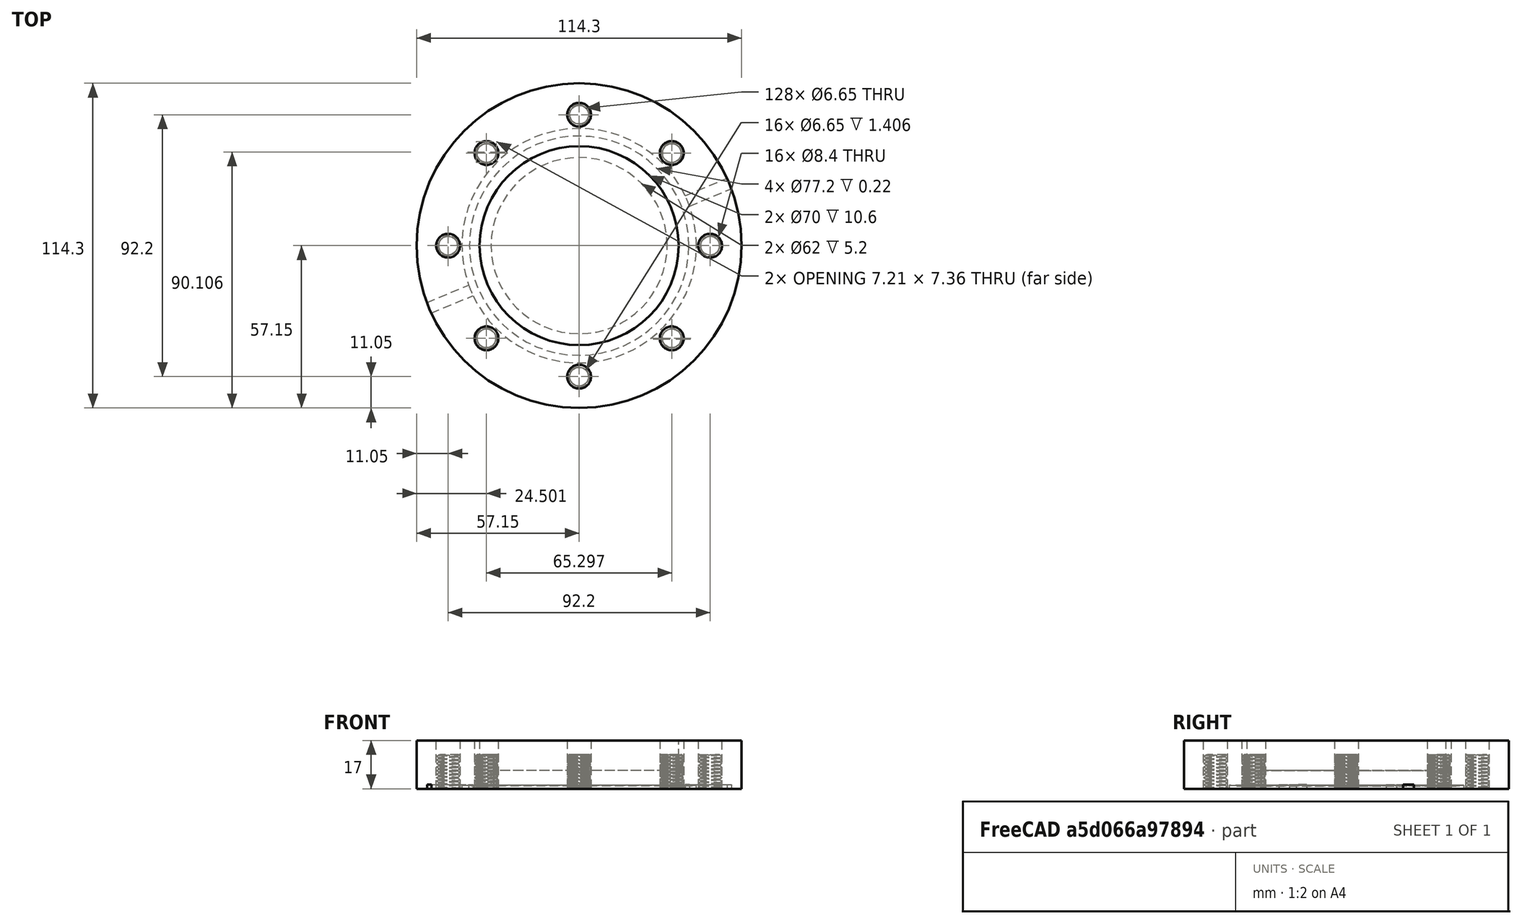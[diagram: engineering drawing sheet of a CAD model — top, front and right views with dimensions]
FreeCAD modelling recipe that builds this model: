
FCSTD DOCUMENT  (FreeCAD 0.21R33668 +7 (Git))
Label: CFFlange
License: All rights reserved
LicenseURL: https://en.wikipedia.org/wiki/All_rights_reserved
objects: Part::Cylinder×22, Part::Cut×22, Part::MultiFuse×10, Part::Box×8, Part::FeaturePython×6, Part::Cone×4, Spreadsheet::Sheet×1
note: 68 computed .brp shape members not serialized (recipe doc carries the construction recipe); baked Part::Feature solids carry a one-line shape summary decoded from their .brp

FEATURE [Spreadsheet::Sheet] Spreadsheet  label="ConflatFlange"
  CF = 5
  cells = A1='CF; B1='Outside Diameter; C1='Maximum tube diameter; D1='Number of bolts; E1='Bolt hole diameter; F1='Tap hole diameter; G1='Bolt Thread (metric); H1='Bot inclination; I1='Bolt Circle; J1='Bolt position tolerance; K1='Seal recess; L1='Knife edge; M1='Pipe attachment depth; N1='Setback (inner rotatable); O1='Thickness; Q1='Calculated Quantities; A2==hiddenref(.CF.String); B2(cf_od)==.B8; C2(cf_maxtubedia)==.C8; D2(cf_nbolts)==.D8; E2(cf_boltdia)==.E8; F2(cf_tapdia)==.F8; G2(cf_boltm)==.G8; H2(cf_boltinclination)==.H8; I2(cf_boltcircle)==.I8; J2(cf_bolttolerance)==.J8; K2(cf_sealrecess)==.K8; L2(cf_knife)==.L8; M2(cf_pipedepth)==.M8; N2(cf_setbackrot)==.N8; O2(cf_thickness)==.O8; Q2='Knife edge width; R2(cf__kfwidth)==(cf_sealrecess - cf_knife) / 2; A3='10; B3=25; C3=12; D3=6; E3=3.3; F3=2.39; G3=3; H3=0.5; I3=17.6; J3=0.1; K3=13.5; L3=10.5; M3=3; N3=0; O3=6; Q3='Knife height; R3(cf__kfheight)==tan(20 * 3.14 / 180) * cf__kfwidth; A4='16; B4=33.8; C4=19.4; D4=6; E4=4.4; F4=3.14; G4=4; H4=0.7; I4=27; J4=0.1; K4=21.4; L4=18.3; M4=3.3; N4=5.9; O4=7; A5='25; B5=54; C5=25.8; D5=4; E5=6.8; F5=4.77; G5=6; H5=1; I5=41.3; J5=0.2; K5=33; L5=27.7; M5=4.3; N5=6; O5=11.5; A6='40; B6=69.9; C6=44.5; D6=6; E6=6.8; F6=4.77; G6=6; H6=1; I6=58.7; J6=0.2; K6=48.3; L6=41.9; M6=4.3; N6=7.7; O6=12.5; A7='50; B7=85.7; C7=51; D7=8; E7=8.4; F7=6.47; G7=8; H7=1.25; I7=72.4; J7=0.2; K7=61.8; L7=55.9; M7=4.9; N7=9.7; O7=16; A8='63; B8=114.3; C8=70; D8=8; E8=8.4; F8=6.47; G8=8; H8=1.25; I8=92.2; J8=0.2; K8=82.5; L8=77.2; M8=6.4; N8=12.7; O8=17; A9='75; B9=117.4; C9=76.2; D9=10; E9=8.4; F9=6.47; G9=8; H9=1.25; I9=102.3; J9=0.2; K9=91.6; L9=85.2; M9=6.5; N9=13; O9=17.5; A10='100; B10=152.4; C10=108; D10=16; E10=8.4; F10=6.47; G10=8; H10=1.25; I10=130.3; J10=0.2; K10=120.6; L10=115.3; M10=7.2; N10=14.3; O10=19.5; A11='125; B11=171.5; C11=127; D11=18; E11=8.4; F11=6.47; G11=8; H11=1.25; I11=151.6; J11=0.2; K11=141.8; L11=136.3; M11=7.2; N11=14.3; O11=21; A12='160; B12=203.2; C12=159; D12=20; E12=8.4; F12=6.47; G12=8; H12=1.25; I12=181; J12=0.2; K12=171.4; L12=166.1; M12=8; N12=15.9; O12=21; A13='200; B13=254; C13=206; D13=24; E13=8.4; F13=6.47; G13=8; H13=1.25; I13=231.8; J13=0.2; K13=222.2; L13=216.9; M13=8.6; N13=17.2; O13=24; +88 more cells
  expr: .CF.Enum = cells[<<A3:|>>]
  expr: .cells.Bind.B2.O2 = tuple(.cells; <<B>> + str(hiddenref(CF) + 3); <<O>> + str(hiddenref(CF) + 3))
FEATURE [Part::Cylinder] Cylinder  label="Blank"
  Angle = 360
  AttacherType = Attacher::AttachEngine3D
  FirstAngle = 0
  Height = 17
  Radius = 57.15
  SecondAngle = 0
  expr: Height = <<ConflatFlange>>.cf_thickness
  expr: Radius = <<ConflatFlange>>.cf_od / 2
FEATURE [Part::Cylinder] Cylinder001  label="SealRecess"
  Angle = 360
  AttacherType = Attacher::AttachEngine3D
  FirstAngle = 0
  Height = 1.2
  Radius = 41.25
  SecondAngle = 0
  expr: Radius = <<ConflatFlange>>.cf_sealrecess / 2
FEATURE [Part::Cut] Cut
  Base = -> Cylinder
  Tool = -> Cylinder001
FEATURE [Part::Cone] Cone
  Angle = 360
  AttacherType = Attacher::AttachEngine3D
  Height = 0.22
  Radius1 = 38.6
  Radius2 = 41.25
  expr: Height = 1.2 - 0.98
  expr: Radius1 = <<ConflatFlange>>.cf_knife / 2
  expr: Radius2 = <<ConflatFlange>>.cf_sealrecess / 2
FEATURE [Part::Cylinder] Cylinder002  label="Cylinder"
  Angle = 360
  AttacherType = Attacher::AttachEngine3D
  FirstAngle = 0
  Height = 0.22
  Radius = 38.6
  SecondAngle = 0
  expr: Height = 1.2 - 0.98
  expr: Radius = <<ConflatFlange>>.cf_knife / 2
FEATURE [Part::Cut] Cut001  label="KnifeEdge"
  Base = -> Cone
  Placement = pos=(0,0,0.98) rot=(0,0,1;0rad)
  Tool = -> Cylinder002
FEATURE [Part::MultiFuse] Fusion  label="UndrilledBlank"
  Shapes = -> [Cut,Cut001]
FEATURE [Part::Cylinder] Cylinder003
  Angle = 360
  AttacherType = Attacher::AttachEngine3D
  FirstAngle = 0
  Height = 17
  Placement = pos=(46.1,0,0) rot=(0,0,1;0rad)
  Radius = 4.2
  SecondAngle = 0
  expr: .Placement.Base.x = <<ConflatFlange>>.cf_boltcircle / 2
  expr: Height = <<ConflatFlange>>.cf_thickness
  expr: Radius = <<ConflatFlange>>.cf_boltdia / 2
FEATURE [Part::FeaturePython] Array  label="BoltHoleArray"  # Draft array (typed FeaturePython)
  AlwaysSyncPlacement = false
  Angle = 360
  ArrayType = 1
  Axis = (0,0,1)
  Base = -> Cylinder003
  Center = (0,0,0)
  Count = 8
  ExpandArray = false
  Fuse = false
  IntervalAxis = (0,0,0)
  IntervalX = (50,0,0)
  IntervalY = (0,50,0)
  IntervalZ = (0,0,50)
  NumberCircles = 3
  NumberPolar = 8
  NumberX = 2
  NumberY = 2
  NumberZ = 1
  PlacementList = 8 placements: [(46.1,0,0),(32.5976,32.5976,0),(0,46.1,0),(-32.5976,32.5976,0),(-46.1,5.64562e-15,0),(-32.5976,-32.5976,0),(-1.02363e-14,-46.1,0),(32.5976,-32.5976,0)]
  RadialDistance = 50
  ScaleList = (8) [(1,1,1),(1,1,1),(1,1,1),(1,1,1),(1,1,1),(1,1,1),(1,1,1),(1,1,1)]
  Symmetry = 1
  TangentialDistance = 25
  expr: NumberPolar = <<ConflatFlange>>.cf_nbolts
FEATURE [Part::Cut] Cut002  label="BlankFlange_NonRotatable_NoGrooves"
  Base = -> Fusion
  Tool = -> Array
FEATURE [Part::Cone] Cone002
  Angle = 360
  AttacherType = Attacher::AttachEngine3D
  Height = 0.22
  Radius1 = 38.6
  Radius2 = 41.25
  expr: Height = 1.2 - 0.98
  expr: Radius1 = <<ConflatFlange>>.cf_knife / 2
  expr: Radius2 = <<ConflatFlange>>.cf_sealrecess / 2
FEATURE [Part::Cylinder] Cylinder010  label="Blank002"
  Angle = 360
  AttacherType = Attacher::AttachEngine3D
  FirstAngle = 0
  Height = 17
  Radius = 57.15
  SecondAngle = 0
  expr: Height = <<ConflatFlange>>.cf_thickness
  expr: Radius = <<ConflatFlange>>.cf_od / 2
FEATURE [Part::Cylinder] Cylinder011  label="SealRecess002"
  Angle = 360
  AttacherType = Attacher::AttachEngine3D
  FirstAngle = 0
  Height = 1.2
  Radius = 41.25
  SecondAngle = 0
  expr: Radius = <<ConflatFlange>>.cf_sealrecess / 2
FEATURE [Part::Cut] Cut008
  Base = -> Cylinder010
  Tool = -> Cylinder011
FEATURE [Part::Cylinder] Cylinder012
  Angle = 360
  AttacherType = Attacher::AttachEngine3D
  FirstAngle = 0
  Height = 0.22
  Radius = 38.6
  SecondAngle = 0
  expr: Height = 1.2 - 0.98
  expr: Radius = <<ConflatFlange>>.cf_knife / 2
FEATURE [Part::Cut] Cut009  label="KnifeEdge002"
  Base = -> Cone002
  Placement = pos=(0,0,0.98) rot=(0,0,1;0rad)
  Tool = -> Cylinder012
FEATURE [Part::MultiFuse] Fusion002  label="UndrilledBlank002"
  Shapes = -> [Cut008,Cut009]
FEATURE [Part::FeaturePython] ScrewTap  label="8x12-ScrewTap"  # Fasteners workbench fastener (typed FeaturePython)
  Placement = pos=(46.1,0,12) rot=(0,0,1;0rad)
  diameter = 29
  diameterCustom = 8
  invert = false
  leftHanded = false
  length = 12
  matchOuter = false
  offset = 0
  pitchCustom = 1.25
  thread = true
  type = 2
  expr: .Placement.Base.x = <<ConflatFlange>>.cf_boltcircle / 2
  expr: .Placement.Base.z = <<ConflatFlange>>.cf_thickness - <<ConflatFlange>>.cf_materialbelowtap
  expr: diameterCustom = <<ConflatFlange>>.cf_boltm
  expr: length = <<ConflatFlange>>.cf_thickness - <<ConflatFlange>>.cf_materialbelowtap
  expr: pitchCustom = <<ConflatFlange>>.cf_boltinclination
FEATURE [Part::FeaturePython] Array002  label="BoltHoleArray002"  # Draft array (typed FeaturePython)
  AlwaysSyncPlacement = false
  Angle = 360
  ArrayType = 1
  Axis = (0,0,1)
  Base = -> ScrewTap
  Center = (0,0,0)
  Count = 8
  ExpandArray = false
  Fuse = false
  IntervalAxis = (0,0,0)
  IntervalX = (50,0,0)
  IntervalY = (0,50,0)
  IntervalZ = (0,0,50)
  NumberCircles = 3
  NumberPolar = 8
  NumberX = 2
  NumberY = 2
  NumberZ = 1
  PlacementList = 8 placements: [(46.1,0,12),(32.5976,32.5976,12),(0,46.1,12),(-32.5976,32.5976,12),(-46.1,5.64562e-15,12),(-32.5976,-32.5976,12),(-1.02363e-14,-46.1,12),(32.5976,-32.5976,12)]
  RadialDistance = 50
  ScaleList = (8) [(1,1,1),(1,1,1),(1,1,1),(1,1,1),(1,1,1),(1,1,1),(1,1,1),(1,1,1)]
  Symmetry = 1
  TangentialDistance = 25
  expr: NumberPolar = <<ConflatFlange>>.cf_nbolts
FEATURE [Part::Cut] Cut010  label="BlankFlange_NonRotatable_Tapped_NoGrooves"
  Base = -> Fusion002
  Tool = -> Array002
FEATURE [Part::Cone] Cone003
  Angle = 360
  AttacherType = Attacher::AttachEngine3D
  Height = 0.22
  Radius1 = 38.6
  Radius2 = 41.25
  expr: Height = 1.2 - 0.98
  expr: Radius1 = <<ConflatFlange>>.cf_knife / 2
  expr: Radius2 = <<ConflatFlange>>.cf_sealrecess / 2
FEATURE [Part::Cylinder] Cylinder013  label="Blank003"
  Angle = 360
  AttacherType = Attacher::AttachEngine3D
  FirstAngle = 0
  Height = 17
  Radius = 57.15
  SecondAngle = 0
  expr: Height = <<ConflatFlange>>.cf_thickness
  expr: Radius = <<ConflatFlange>>.cf_od / 2
FEATURE [Part::Cylinder] Cylinder014  label="SealRecess003"
  Angle = 360
  AttacherType = Attacher::AttachEngine3D
  FirstAngle = 0
  Height = 1.2
  Radius = 41.25
  SecondAngle = 0
  expr: Radius = <<ConflatFlange>>.cf_sealrecess / 2
FEATURE [Part::Cut] Cut011
  Base = -> Cylinder013
  Tool = -> Cylinder014
FEATURE [Part::Cylinder] Cylinder015
  Angle = 360
  AttacherType = Attacher::AttachEngine3D
  FirstAngle = 0
  Height = 0.22
  Radius = 38.6
  SecondAngle = 0
  expr: Height = 1.2 - 0.98
  expr: Radius = <<ConflatFlange>>.cf_knife / 2
FEATURE [Part::Cut] Cut012  label="KnifeEdge003"
  Base = -> Cone003
  Placement = pos=(0,0,0.98) rot=(0,0,1;0rad)
  Tool = -> Cylinder015
FEATURE [Part::MultiFuse] Fusion003  label="UndrilledBlank003"
  Shapes = -> [Cut011,Cut012]
FEATURE [Part::FeaturePython] ScrewTap001  label="8x12-ScrewTap001"  # Fasteners workbench fastener (typed FeaturePython)
  Placement = pos=(46.1,0,12) rot=(0,0,1;0rad)
  diameter = 29
  diameterCustom = 8
  invert = false
  leftHanded = false
  length = 12
  matchOuter = false
  offset = 0
  pitchCustom = 1.25
  thread = true
  type = 2
  expr: .Placement.Base.x = <<ConflatFlange>>.cf_boltcircle / 2
  expr: .Placement.Base.z = <<ConflatFlange>>.cf_thickness - <<ConflatFlange>>.cf_materialbelowtap
  expr: diameterCustom = <<ConflatFlange>>.cf_boltm
  expr: length = <<ConflatFlange>>.cf_thickness - <<ConflatFlange>>.cf_materialbelowtap
  expr: pitchCustom = <<ConflatFlange>>.cf_boltinclination
FEATURE [Part::FeaturePython] Array003  label="BoltHoleArray003"  # Draft array (typed FeaturePython)
  AlwaysSyncPlacement = false
  Angle = 360
  ArrayType = 1
  Axis = (0,0,1)
  Base = -> ScrewTap001
  Center = (0,0,0)
  Count = 8
  ExpandArray = false
  Fuse = false
  IntervalAxis = (0,0,0)
  IntervalX = (50,0,0)
  IntervalY = (0,50,0)
  IntervalZ = (0,0,50)
  NumberCircles = 3
  NumberPolar = 8
  NumberX = 2
  NumberY = 2
  NumberZ = 1
  PlacementList = 8 placements: [(46.1,0,12),(32.5976,32.5976,12),(0,46.1,12),(-32.5976,32.5976,12),(-46.1,5.64562e-15,12),(-32.5976,-32.5976,12),(-1.02363e-14,-46.1,12),(32.5976,-32.5976,12)]
  RadialDistance = 50
  ScaleList = (8) [(1,1,1),(1,1,1),(1,1,1),(1,1,1),(1,1,1),(1,1,1),(1,1,1),(1,1,1)]
  Symmetry = 1
  TangentialDistance = 25
  expr: NumberPolar = <<ConflatFlange>>.cf_nbolts
FEATURE [Part::Cut] Cut013  label="BlankFlange_NonRotatable_Tapped001"
  Base = -> Fusion003
  Tool = -> Array003
FEATURE [Part::Cylinder] Cylinder016
  Angle = 360
  AttacherType = Attacher::AttachEngine3D
  FirstAngle = 0
  Height = 10.6
  Placement = pos=(0,0,6.4) rot=(0,0,1;0rad)
  Radius = 35
  SecondAngle = 0
  expr: .Placement.Base.z = <<ConflatFlange>>.cf_pipedepth
  expr: Height = <<ConflatFlange>>.cf_thickness - <<ConflatFlange>>.cf_pipedepth
  expr: Radius = <<ConflatFlange>>.cf_maxtubedia / 2
FEATURE [Part::Cylinder] Cylinder017
  Angle = 360
  AttacherType = Attacher::AttachEngine3D
  FirstAngle = 0
  Height = 17
  Radius = 31
  SecondAngle = 0
  expr: Height = <<ConflatFlange>>.cf_thickness
  expr: Radius = <<ConflatFlange>>.cf_maxtubedia / 2 - 2 * <<ConflatFlange>>.cf_pipe_wallwidth
FEATURE [Part::MultiFuse] Fusion004
  Shapes = -> [Cylinder016,Cylinder017]
FEATURE [Part::Cut] Cut014  label="WeldFlange_NonRotatable_Tapped_NoGroove"
  Base = -> Cut013
  Tool = -> Fusion004
FEATURE [Part::Cylinder] Cylinder018
  Angle = 360
  AttacherType = Attacher::AttachEngine3D
  FirstAngle = 0
  Height = 10.6
  Placement = pos=(0,0,6.4) rot=(0,0,1;0rad)
  Radius = 35
  SecondAngle = 0
  expr: .Placement.Base.z = <<ConflatFlange>>.cf_pipedepth
  expr: Height = <<ConflatFlange>>.cf_thickness - <<ConflatFlange>>.cf_pipedepth
  expr: Radius = <<ConflatFlange>>.cf_maxtubedia / 2
FEATURE [Part::Cylinder] Cylinder019
  Angle = 360
  AttacherType = Attacher::AttachEngine3D
  FirstAngle = 0
  Height = 17
  Radius = 31
  SecondAngle = 0
  expr: Height = <<ConflatFlange>>.cf_thickness
  expr: Radius = <<ConflatFlange>>.cf_maxtubedia / 2 - 2 * <<ConflatFlange>>.cf_pipe_wallwidth
FEATURE [Part::Cone] Cone004
  Angle = 360
  AttacherType = Attacher::AttachEngine3D
  Height = 0.22
  Radius1 = 38.6
  Radius2 = 41.25
  expr: Height = 1.2 - 0.98
  expr: Radius1 = <<ConflatFlange>>.cf_knife / 2
  expr: Radius2 = <<ConflatFlange>>.cf_sealrecess / 2
FEATURE [Part::Cylinder] Cylinder020  label="Blank004"
  Angle = 360
  AttacherType = Attacher::AttachEngine3D
  FirstAngle = 0
  Height = 17
  Radius = 57.15
  SecondAngle = 0
  expr: Height = <<ConflatFlange>>.cf_thickness
  expr: Radius = <<ConflatFlange>>.cf_od / 2
FEATURE [Part::Cylinder] Cylinder021  label="SealRecess004"
  Angle = 360
  AttacherType = Attacher::AttachEngine3D
  FirstAngle = 0
  Height = 1.2
  Radius = 41.25
  SecondAngle = 0
  expr: Radius = <<ConflatFlange>>.cf_sealrecess / 2
FEATURE [Part::Cut] Cut015
  Base = -> Cylinder020
  Tool = -> Cylinder021
FEATURE [Part::Cylinder] Cylinder022
  Angle = 360
  AttacherType = Attacher::AttachEngine3D
  FirstAngle = 0
  Height = 0.22
  Radius = 38.6
  SecondAngle = 0
  expr: Height = 1.2 - 0.98
  expr: Radius = <<ConflatFlange>>.cf_knife / 2
FEATURE [Part::Cut] Cut016  label="KnifeEdge004"
  Base = -> Cone004
  Placement = pos=(0,0,0.98) rot=(0,0,1;0rad)
  Tool = -> Cylinder022
FEATURE [Part::Cylinder] Cylinder023
  Angle = 360
  AttacherType = Attacher::AttachEngine3D
  FirstAngle = 0
  Height = 17
  Placement = pos=(46.1,0,0) rot=(0,0,1;0rad)
  Radius = 4.2
  SecondAngle = 0
  expr: .Placement.Base.x = <<ConflatFlange>>.cf_boltcircle / 2
  expr: Height = <<ConflatFlange>>.cf_thickness
  expr: Radius = <<ConflatFlange>>.cf_boltdia / 2
FEATURE [Part::FeaturePython] Array004  label="BoltHoleArray004"  # Draft array (typed FeaturePython)
  AlwaysSyncPlacement = false
  Angle = 360
  ArrayType = 1
  Axis = (0,0,1)
  Base = -> Cylinder023
  Center = (0,0,0)
  Count = 8
  ExpandArray = false
  Fuse = false
  IntervalAxis = (0,0,0)
  IntervalX = (50,0,0)
  IntervalY = (0,50,0)
  IntervalZ = (0,0,50)
  NumberCircles = 3
  NumberPolar = 8
  NumberX = 2
  NumberY = 2
  NumberZ = 1
  PlacementList = 8 placements: [(46.1,0,0),(32.5976,32.5976,0),(0,46.1,0),(-32.5976,32.5976,0),(-46.1,5.64562e-15,0),(-32.5976,-32.5976,0),(-1.02363e-14,-46.1,0),(32.5976,-32.5976,0)]
  RadialDistance = 50
  ScaleList = (8) [(1,1,1),(1,1,1),(1,1,1),(1,1,1),(1,1,1),(1,1,1),(1,1,1),(1,1,1)]
  Symmetry = 1
  TangentialDistance = 25
  expr: NumberPolar = <<ConflatFlange>>.cf_nbolts
FEATURE [Part::MultiFuse] Fusion005  label="UndrilledBlank004"
  Shapes = -> [Cut015,Cut016]
FEATURE [Part::Cut] Cut017  label="BlankFlange_NonRotatable002"
  Base = -> Fusion005
  Tool = -> Array004
FEATURE [Part::MultiFuse] Fusion006
  Shapes = -> [Cylinder019,Cylinder018]
FEATURE [Part::Cut] Cut018  label="WeldFlange_NonRotatable_NoGrooves"
  Base = -> Cut017
  Tool = -> Fusion006
FEATURE [Part::Box] Box  label="Cube"
  AttacherType = Attacher::AttachEngine3D
  Height = 1.5
  Length = 16.9
  Placement = pos=(40.75,-2,0) rot=(0,0,1;0rad)
  Width = 4
  expr: .Placement.Base.x = <<ConflatFlange>>.cf_sealrecess / 2 - 0.5
  expr: .Placement.Base.y = -2
  expr: Length = (<<ConflatFlange>>.cf_od - <<ConflatFlange>>.cf_sealrecess) / 2 + 1
FEATURE [Part::Box] Box001  label="Cube001"
  AttacherType = Attacher::AttachEngine3D
  Height = 1.5
  Length = 16.9
  Placement = pos=(-57.65,-2,0) rot=(0,0,1;0rad)
  Width = 4
  expr: .Placement.Base.x = -<<ConflatFlange>>.cf_sealrecess / 2 + 0.5 - ((<<ConflatFlange>>.cf_od - <<ConflatFlange>>.cf_sealrecess) / 2 + 1)
  expr: .Placement.Base.y = -2
  expr: Length = (<<ConflatFlange>>.cf_od - <<ConflatFlange>>.cf_sealrecess) / 2 + 1
FEATURE [Part::MultiFuse] Fusion007
  Placement = pos=(0,0,0) rot=(0,0,1;0.392699rad)
  Shapes = -> [Box001,Box]
  expr: .Placement.Rotation.Angle = 360 / (<<ConflatFlange>>.cf_nbolts * 2)
FEATURE [Part::Cylinder] Cylinder024
  Angle = 360
  AttacherType = Attacher::AttachEngine3D
  FirstAngle = 0
  Height = 1.5
  Radius = 41.25
  SecondAngle = 0
  expr: Radius = <<ConflatFlange>>.cf_sealrecess / 2
FEATURE [Part::Cut] Cut019  label="LeakTestGrooves01"
  Base = -> Fusion007
  Tool = -> Cylinder024
FEATURE [Part::Cut] Cut020  label="BlankFlange_NonRotatable"
  Base = -> Cut002
  Tool = -> Cut019
FEATURE [Part::Box] Box002  label="Cube002"
  AttacherType = Attacher::AttachEngine3D
  Height = 1.5
  Length = 16.9
  Placement = pos=(40.75,-2,0) rot=(0,0,1;0rad)
  Width = 4
  expr: .Placement.Base.x = <<ConflatFlange>>.cf_sealrecess / 2 - 0.5
  expr: .Placement.Base.y = -2
  expr: Length = (<<ConflatFlange>>.cf_od - <<ConflatFlange>>.cf_sealrecess) / 2 + 1
FEATURE [Part::Box] Box003  label="Cube003"
  AttacherType = Attacher::AttachEngine3D
  Height = 1.5
  Length = 16.9
  Placement = pos=(-57.65,-2,0) rot=(0,0,1;0rad)
  Width = 4
  expr: .Placement.Base.x = -<<ConflatFlange>>.cf_sealrecess / 2 + 0.5 - ((<<ConflatFlange>>.cf_od - <<ConflatFlange>>.cf_sealrecess) / 2 + 1)
  expr: .Placement.Base.y = -2
  expr: Length = (<<ConflatFlange>>.cf_od - <<ConflatFlange>>.cf_sealrecess) / 2 + 1
FEATURE [Part::Cylinder] Cylinder025
  Angle = 360
  AttacherType = Attacher::AttachEngine3D
  FirstAngle = 0
  Height = 1.5
  Radius = 41.25
  SecondAngle = 0
  expr: Radius = <<ConflatFlange>>.cf_sealrecess / 2
FEATURE [Part::MultiFuse] Fusion008
  Placement = pos=(0,0,0) rot=(0,0,1;0.392699rad)
  Shapes = -> [Box003,Box002]
  expr: .Placement.Rotation.Angle = 360 / (<<ConflatFlange>>.cf_nbolts * 2)
FEATURE [Part::Cut] Cut021  label="LeakTestGrooves02"
  Base = -> Fusion008
  Tool = -> Cylinder025
FEATURE [Part::Box] Box004  label="Cube004"
  AttacherType = Attacher::AttachEngine3D
  Height = 1.5
  Length = 16.9
  Placement = pos=(40.75,-2,0) rot=(0,0,1;0rad)
  Width = 4
  expr: .Placement.Base.x = <<ConflatFlange>>.cf_sealrecess / 2 - 0.5
  expr: .Placement.Base.y = -2
  expr: Length = (<<ConflatFlange>>.cf_od - <<ConflatFlange>>.cf_sealrecess) / 2 + 1
FEATURE [Part::Box] Box005  label="Cube005"
  AttacherType = Attacher::AttachEngine3D
  Height = 1.5
  Length = 16.9
  Placement = pos=(-57.65,-2,0) rot=(0,0,1;0rad)
  Width = 4
  expr: .Placement.Base.x = -<<ConflatFlange>>.cf_sealrecess / 2 + 0.5 - ((<<ConflatFlange>>.cf_od - <<ConflatFlange>>.cf_sealrecess) / 2 + 1)
  expr: .Placement.Base.y = -2
  expr: Length = (<<ConflatFlange>>.cf_od - <<ConflatFlange>>.cf_sealrecess) / 2 + 1
FEATURE [Part::Cylinder] Cylinder026
  Angle = 360
  AttacherType = Attacher::AttachEngine3D
  FirstAngle = 0
  Height = 1.5
  Radius = 41.25
  SecondAngle = 0
  expr: Radius = <<ConflatFlange>>.cf_sealrecess / 2
FEATURE [Part::MultiFuse] Fusion009
  Placement = pos=(0,0,0) rot=(0,0,1;0.392699rad)
  Shapes = -> [Box005,Box004]
  expr: .Placement.Rotation.Angle = 360 / (<<ConflatFlange>>.cf_nbolts * 2)
FEATURE [Part::Cut] Cut022  label="LeakTestGrooves03"
  Base = -> Fusion009
  Tool = -> Cylinder026
FEATURE [Part::Box] Box006  label="Cube006"
  AttacherType = Attacher::AttachEngine3D
  Height = 1.5
  Length = 16.9
  Placement = pos=(40.75,-2,0) rot=(0,0,1;0rad)
  Width = 4
  expr: .Placement.Base.x = <<ConflatFlange>>.cf_sealrecess / 2 - 0.5
  expr: .Placement.Base.y = -2
  expr: Length = (<<ConflatFlange>>.cf_od - <<ConflatFlange>>.cf_sealrecess) / 2 + 1
FEATURE [Part::Box] Box007  label="Cube007"
  AttacherType = Attacher::AttachEngine3D
  Height = 1.5
  Length = 16.9
  Placement = pos=(-57.65,-2,0) rot=(0,0,1;0rad)
  Width = 4
  expr: .Placement.Base.x = -<<ConflatFlange>>.cf_sealrecess / 2 + 0.5 - ((<<ConflatFlange>>.cf_od - <<ConflatFlange>>.cf_sealrecess) / 2 + 1)
  expr: .Placement.Base.y = -2
  expr: Length = (<<ConflatFlange>>.cf_od - <<ConflatFlange>>.cf_sealrecess) / 2 + 1
FEATURE [Part::Cylinder] Cylinder027
  Angle = 360
  AttacherType = Attacher::AttachEngine3D
  FirstAngle = 0
  Height = 1.5
  Radius = 41.25
  SecondAngle = 0
  expr: Radius = <<ConflatFlange>>.cf_sealrecess / 2
FEATURE [Part::MultiFuse] Fusion010
  Placement = pos=(0,0,0) rot=(0,0,1;0.392699rad)
  Shapes = -> [Box007,Box006]
  expr: .Placement.Rotation.Angle = 360 / (<<ConflatFlange>>.cf_nbolts * 2)
FEATURE [Part::Cut] Cut023  label="LeakTestGrooves04"
  Base = -> Fusion010
  Tool = -> Cylinder027
FEATURE [Part::Cut] Cut024  label="WeldFlange_NonRotatable"
  Base = -> Cut018
  Tool = -> Cut021
FEATURE [Part::Cut] Cut025  label="BlankFlange_NonRotatable_Tapped"
  Base = -> Cut010
  Tool = -> Cut022
FEATURE [Part::Cut] Cut026  label="WeldFlange_NonRotatable_Tapped"
  Base = -> Cut014
  Tool = -> Cut023
